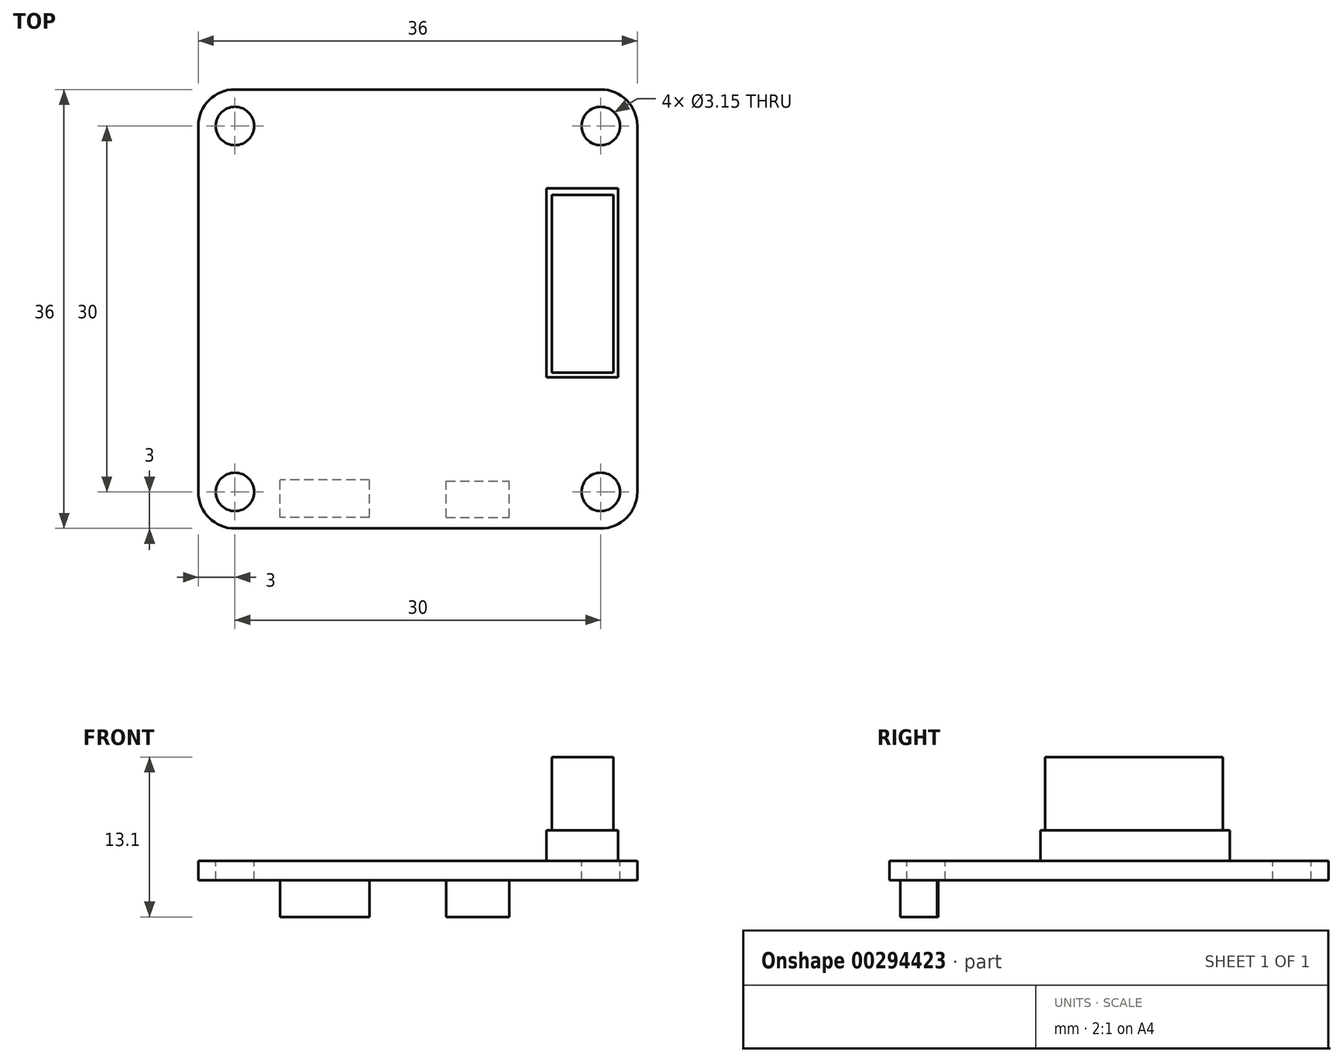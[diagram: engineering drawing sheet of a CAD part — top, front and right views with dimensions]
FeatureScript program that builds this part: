
annotation { "Feature Type Name" : "Feature", "Feature Type Description" : "" }
export const myFeature = defineFeature(function(context is Context, id is Id, definition is map)
    precondition{}
    {
        {
            var Q0;
            Q0=qCreatedBy(makeId("Top.planeOp"),FACE);
            var sketch = newSketch(context, id + "F0", { "sketchPlane" : qUnion([Q0])});
            skLineSegment(sketch, "E0.bottom", {"start": v(-18, 18) * mm, "end": v(18, 18) * mm});
            skLineSegment(sketch, "E0.top", {"start": v(-18, -18) * mm, "end": v(18, -18) * mm});
            skLineSegment(sketch, "E0.left", {"start": v(-18, 18) * mm, "end": v(-18, -18) * mm});
            skLineSegment(sketch, "E0.right", {"start": v(18, 18) * mm, "end": v(18, -18) * mm});
            skPoint(sketch, "E0.middle", {"position": v(0, 0) * mm});
            skLineSegment(sketch, "E1.bottom", {"start": v(-15, 15) * mm, "end": v(15, 15) * mm, "construction": true});
            skLineSegment(sketch, "E1.top", {"start": v(-15, -15) * mm, "end": v(15, -15) * mm, "construction": true});
            skLineSegment(sketch, "E1.left", {"start": v(-15, 15) * mm, "end": v(-15, -15) * mm, "construction": true});
            skLineSegment(sketch, "E1.right", {"start": v(15, 15) * mm, "end": v(15, -15) * mm, "construction": true});
            skSolve(sketch);
        }
        {
            var Q0;
            Q0 = qSketchRegion(id + "F0", true);
            extrude(context, id + "F1", {"entities" : qUnion([Q0]), "oppositeDirection" : true, "depth" : 1.6 * mm});
        }
        {
            var Q0;
            Q0=makeQuery(id+"F1.opExtrude","SWEPT_EDGE",EDGE,{"disambiguationData":[OSD([sQuery(id+"F0.wireOp",EDGE,"E0.top"),sQuery(id+"F0.wireOp",EDGE,"E0.right")])]});
            var Q1;
            Q1=makeQuery(id+"F1.opExtrude","SWEPT_EDGE",EDGE,{"disambiguationData":[OSD([sQuery(id+"F0.wireOp",EDGE,"E0.top"),sQuery(id+"F0.wireOp",EDGE,"E0.left")])]});
            var Q2;
            Q2=makeQuery(id+"F1.opExtrude","SWEPT_EDGE",EDGE,{"disambiguationData":[OSD([sQuery(id+"F0.wireOp",EDGE,"E0.bottom"),sQuery(id+"F0.wireOp",EDGE,"E0.right")])]});
            var Q3;
            Q3=makeQuery(id+"F1.opExtrude","SWEPT_EDGE",EDGE,{"disambiguationData":[OSD([sQuery(id+"F0.wireOp",EDGE,"E0.bottom"),sQuery(id+"F0.wireOp",EDGE,"E0.left")])]});
            fillet(context, id + "F2", {"entities" : qUnion([Q0, Q1, Q2, Q3]), "radius" : 3 * mm, "tangentPropagation" : true, "allowEdgeOverflow" : false});
        }
        {
            var Q0;
            Q0=sQuery(id+"F0.wireOp",VERTEX,"E1.left.start");
            var Q1;
            Q1=sQuery(id+"F0.wireOp",VERTEX,"E1.bottom.end");
            var Q2;
            Q2=sQuery(id+"F0.wireOp",VERTEX,"E1.top.end");
            var Q3;
            Q3=sQuery(id+"F0.wireOp",VERTEX,"E1.top.start");
            var Q4;
            Q4=makeQuery(id+"F1.opExtrude","SWEPT_BODY",BODY,{"disambiguationData":[OSD([sQuery(id+"F0.wireOp",EDGE,"E0.bottom"),sQuery(id+"F0.wireOp",EDGE,"E0.top"),sQuery(id+"F0.wireOp",EDGE,"E0.left"),sQuery(id+"F0.wireOp",EDGE,"E0.right")])]});
            hole(context, id + "F3", {"style" : HoleStyle.SIMPLE, "endStyle" : HoleEndStyle.THROUGH, "standardTappedOrClearance" : lookupTablePath({ "standard" : "ISO", "fit" : "Close", "size" : "M3", "type" : "Clearance" }), "standardBlindInLast" : lookupTablePath({ "fit" : "Close", "standard" : "ISO", "size" : "M3", "type" : "Clearance" }), "holeDiameter" : 3.15 * mm, "tappedDepth" : 12.7 * mm, "tapClearance" : 3, "locations" : qUnion([Q0, Q1, Q2, Q3]), "scope" : qUnion([Q4])});
        }
        {
            var Q0;
            Q0=makeQuery(id+"F1.opExtrude","CAP_FACE",FACE,{"disambiguationData":[OSD([sQuery(id+"F0.wireOp",EDGE,"E0.bottom"),sQuery(id+"F0.wireOp",EDGE,"E0.top"),sQuery(id+"F0.wireOp",EDGE,"E0.left"),sQuery(id+"F0.wireOp",EDGE,"E0.right")])],"isStart":false});
            var sketch = newSketch(context, id + "F4", { "sketchPlane" : qUnion([Q0])});
            skLineSegment(sketch, "E2.bottom", {"start": v(2.33, 17.1) * mm, "end": v(7.5, 17.1) * mm});
            skLineSegment(sketch, "E2.top", {"start": v(2.33, 14.1) * mm, "end": v(7.5, 14.1) * mm});
            skLineSegment(sketch, "E2.left", {"start": v(2.33, 17.1) * mm, "end": v(2.33, 14.1) * mm});
            skLineSegment(sketch, "E2.right", {"start": v(7.5, 17.1) * mm, "end": v(7.5, 14.1) * mm});
            skLineSegment(sketch, "E3.bottom", {"start": v(-3.97, 17.1) * mm, "end": v(-11.3, 17.1) * mm});
            skLineSegment(sketch, "E3.top", {"start": v(-3.97, 14) * mm, "end": v(-11.3, 14) * mm});
            skLineSegment(sketch, "E3.left", {"start": v(-3.97, 17.1) * mm, "end": v(-3.97, 14) * mm});
            skLineSegment(sketch, "E3.right", {"start": v(-11.3, 17.1) * mm, "end": v(-11.3, 14) * mm});
            skSolve(sketch);
        }
        {
            var Q0;
            Q0 = qSketchRegion(id + "F4", true);
            extrude(context, id + "F5", {"entities" : qUnion([Q0]), "operationType" : NewBodyOperationType.ADD, "depth" : 3 * mm});
        }
        {
            var Q0;
            Q0=makeQuery(id+"F0.imprint","IMPRINT",FACE,{"disambiguationData":[TD([[makeQuery(id+"F0.imprint","IMPRINT",EDGE,{"derivedFrom":sQuery(id+"F0.wireOp",EDGE,"E0.bottom")}),-1.0]])]});
            var sketch = newSketch(context, id + "F6", { "sketchPlane" : qUnion([Q0])});
            skLineSegment(sketch, "E4.bottom", {"start": v(16.42, 9.9) * mm, "end": v(10.55, 9.9) * mm});
            skLineSegment(sketch, "E4.top", {"start": v(16.42, -5.62) * mm, "end": v(10.55, -5.62) * mm});
            skLineSegment(sketch, "E4.left", {"start": v(16.42, 9.9) * mm, "end": v(16.42, -5.62) * mm});
            skLineSegment(sketch, "E4.right", {"start": v(10.55, 9.9) * mm, "end": v(10.55, -5.62) * mm});
            skSolve(sketch);
        }
        {
            var Q0;
            Q0 = qSketchRegion(id + "F6", true);
            extrude(context, id + "F7", {"entities" : qUnion([Q0]), "operationType" : NewBodyOperationType.ADD, "depth" : 2.5 * mm});
        }
        {
            var Q0;
            Q0=makeQuery(id+"F7.opExtrude","CAP_FACE",FACE,{"disambiguationData":[OSD([sQuery(id+"F6.wireOp",EDGE,"E4.bottom"),sQuery(id+"F6.wireOp",EDGE,"E4.top"),sQuery(id+"F6.wireOp",EDGE,"E4.left"),sQuery(id+"F6.wireOp",EDGE,"E4.right")])],"isStart":false});
            var sketch = newSketch(context, id + "F8", { "sketchPlane" : qUnion([Q0])});
            skLineSegment(sketch, "E5.bottom", {"start": v(11, 9.35) * mm, "end": v(16.04, 9.35) * mm});
            skLineSegment(sketch, "E5.top", {"start": v(11, -5.23) * mm, "end": v(16.04, -5.23) * mm});
            skLineSegment(sketch, "E5.left", {"start": v(11, 9.35) * mm, "end": v(11, -5.23) * mm});
            skLineSegment(sketch, "E5.right", {"start": v(16.04, 9.35) * mm, "end": v(16.04, -5.23) * mm});
            skSolve(sketch);
        }
        {
            var Q0;
            Q0=makeQuery(id+"F8.imprint","IMPRINT",FACE,{"disambiguationData":[TD([[makeQuery(id+"F8.imprint","IMPRINT",EDGE,{"derivedFrom":sQuery(id+"F8.wireOp",EDGE,"E5.bottom")}),-1.0]])]});
            extrude(context, id + "F9", {"entities" : qUnion([Q0]), "operationType" : NewBodyOperationType.ADD, "depth" : 6 * mm});
        }
    });
